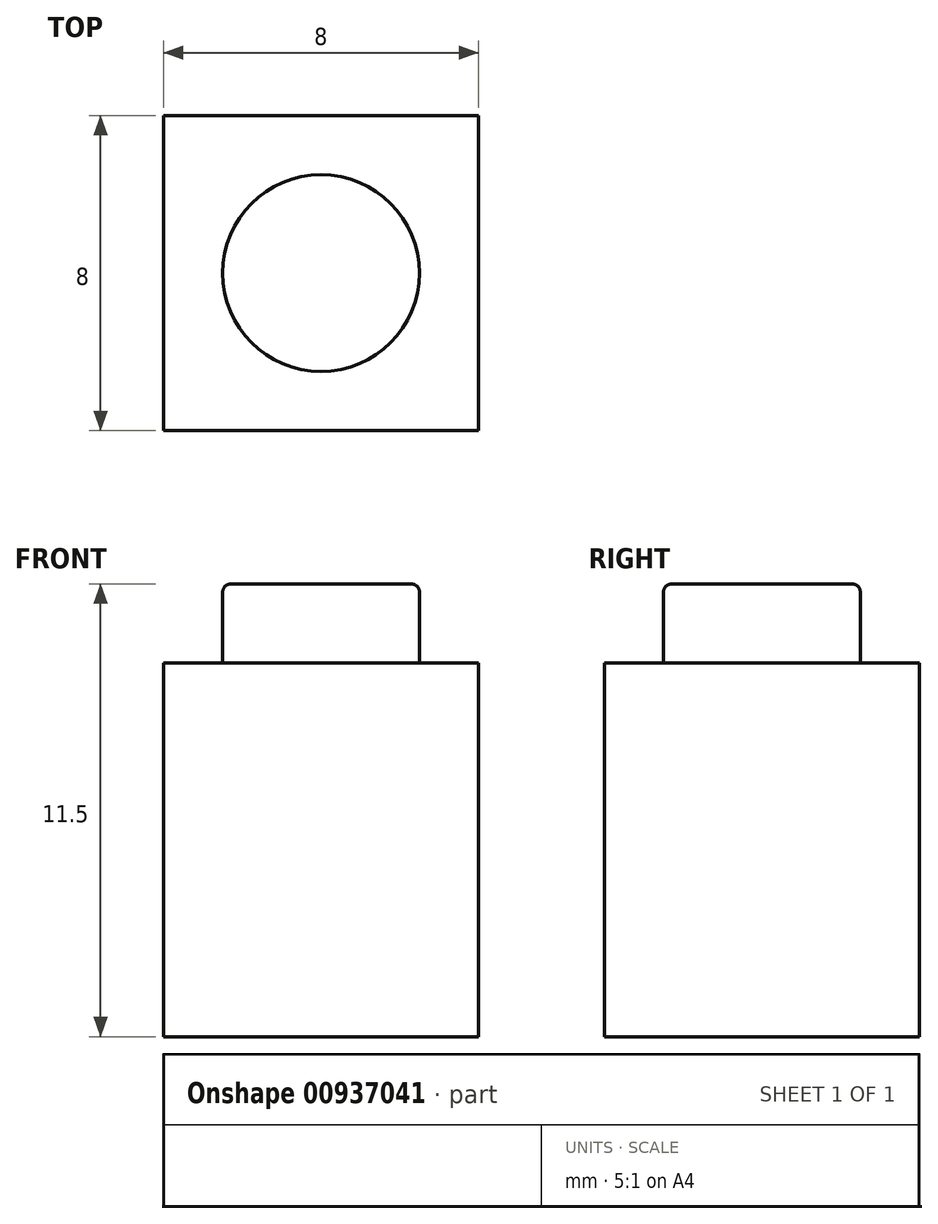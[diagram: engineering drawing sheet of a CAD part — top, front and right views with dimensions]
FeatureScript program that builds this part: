
annotation { "Feature Type Name" : "Feature", "Feature Type Description" : "" }
export const myFeature = defineFeature(function(context is Context, id is Id, definition is map)
    precondition{}
    {
        {
            var Q0;
            Q0=qCreatedBy(makeId("Front.planeOp"),FACE);
            var sketch = newSketch(context, id + "F0", { "sketchPlane" : qUnion([Q0])});
            skLineSegment(sketch, "E0.bottom", {"start": v(4, 4.75) * mm, "end": v(-4, 4.75) * mm});
            skLineSegment(sketch, "E0.top", {"start": v(4, -4.75) * mm, "end": v(-4, -4.75) * mm});
            skLineSegment(sketch, "E0.left", {"start": v(4, 4.75) * mm, "end": v(4, -4.75) * mm});
            skLineSegment(sketch, "E0.right", {"start": v(-4, 4.75) * mm, "end": v(-4, -4.75) * mm});
            skPoint(sketch, "E0.middle", {"position": v(0, 0) * mm});
            skLineSegment(sketch, "E1.bottom", {"start": v(-2.5, 6.75) * mm, "end": v(0, 6.75) * mm});
            skLineSegment(sketch, "E1.top", {"start": v(-2.5, 4.75) * mm, "end": v(2.5, 4.75) * mm});
            skLineSegment(sketch, "E1.left", {"start": v(-2.5, 6.75) * mm, "end": v(-2.5, 4.75) * mm});
            skLineSegment(sketch, "E2", {"start": v(0, 6.75) * mm, "end": v(0, -4.75) * mm});
            skPoint(sketch, "E1.right.start.orphan", {"position": v(2.5, 6.75) * mm});
            skSolve(sketch);
        }
        {
            var Q0;
            {var subQ4=sQuery(id+"F0.wireOp",EDGE,"E1.bottom");Q0=makeQuery(id+"F0.imprint","IMPRINT",FACE,{"disambiguationData":[TD([[makeQuery(id+"F0.imprint","IMPRINT",EDGE,{"derivedFrom":subQ4}),-1.0]])]});}
            var Q1;
            Q1=sQuery(id+"F0.wireOp",EDGE,"E2");
            revolve(context, id + "F1", {"surfaceOperationType" : NewSurfaceOperationType.NEW, "entities" : qUnion([Q0]), "axis" : qUnion([Q1]), "revolveType" : RevolveType.FULL});
        }
        {
            var Q0;
            {var subQ3=sQuery(id+"F0.wireOp",EDGE,"E0.left");Q0=makeQuery(id+"F0.imprint","IMPRINT",FACE,{"disambiguationData":[TD([[makeQuery(id+"F0.imprint","IMPRINT",EDGE,{"derivedFrom":subQ3}),-1.0]])]});}
            var Q1;
            {var subQ3=sQuery(id+"F0.wireOp",EDGE,"E0.right");Q1=makeQuery(id+"F0.imprint","IMPRINT",FACE,{"disambiguationData":[TD([[makeQuery(id+"F0.imprint","IMPRINT",EDGE,{"derivedFrom":subQ3}),1.0]])]});}
            extrude(context, id + "F2", {"entities" : qUnion([Q0, Q1]), "operationType" : NewBodyOperationType.ADD, "depth" : 8 * mm, "offsetDistance" : 25.4 * mm, "symmetric" : true});
        }
        {
            var Q0;
            Q0=makeQuery(id+"F1.opRevolve","SWEPT_EDGE",EDGE,{"disambiguationData":[OSD([sQuery(id+"F0.wireOp",EDGE,"E1.bottom"),sQuery(id+"F0.wireOp",EDGE,"E1.left")])]});
            fillet(context, id + "F3", {"entities" : qUnion([Q0]), "radius" : 0.2 * mm, "tangentPropagation" : true, "allowEdgeOverflow" : false});
        }
    });
